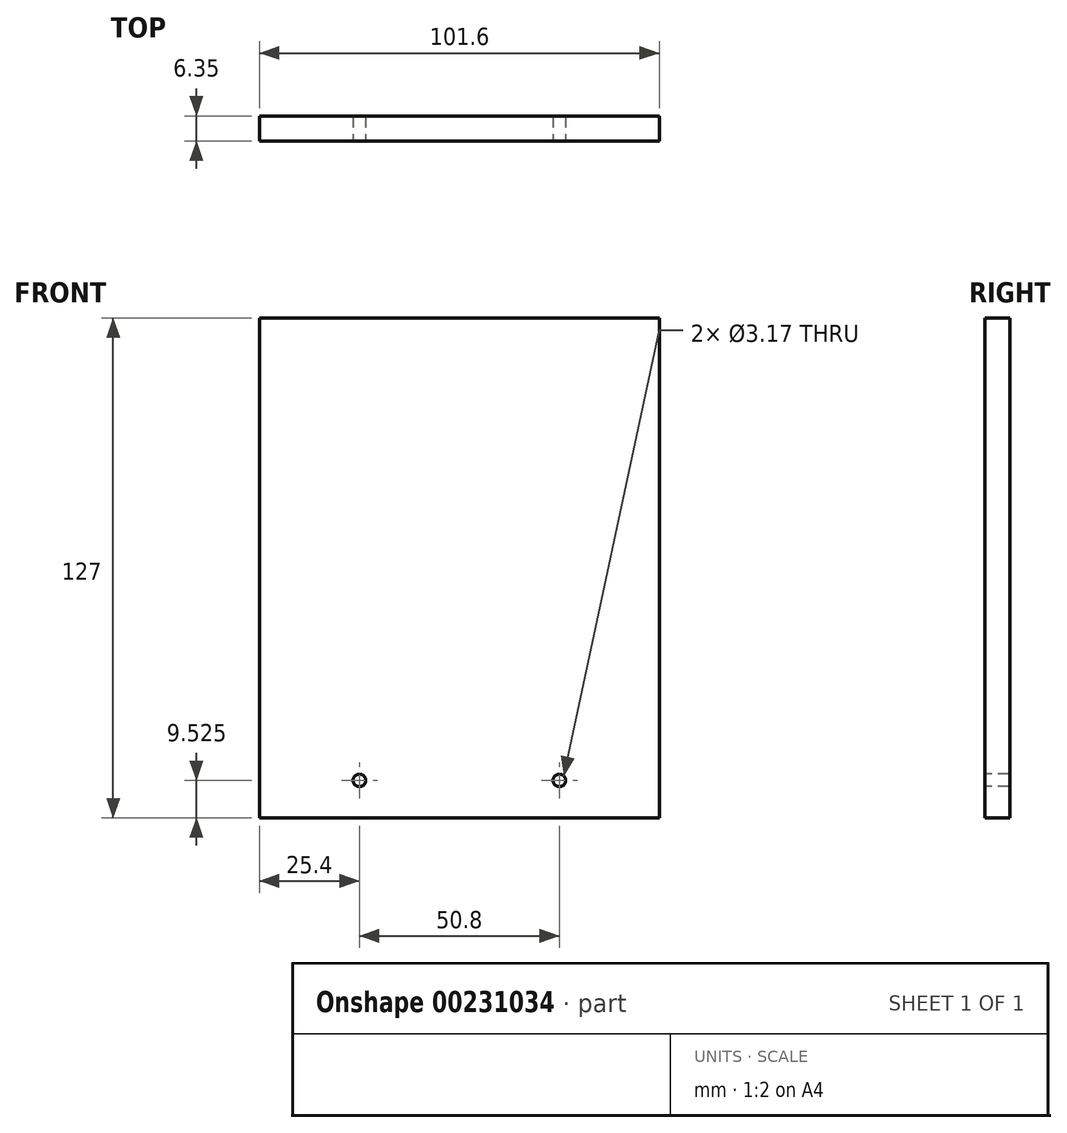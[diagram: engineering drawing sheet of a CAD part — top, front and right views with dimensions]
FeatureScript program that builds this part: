
annotation { "Feature Type Name" : "Feature", "Feature Type Description" : "" }
export const myFeature = defineFeature(function(context is Context, id is Id, definition is map)
    precondition{}
    {
        {
            var Q0;
            Q0=qCreatedBy(makeId("Front.planeOp"),FACE);
            var sketch = newSketch(context, id + "F0", { "sketchPlane" : qUnion([Q0])});
            skLineSegment(sketch, "E0.bottom", {"start": v(50.8, 63.5) * mm, "end": v(-50.8, 63.5) * mm});
            skLineSegment(sketch, "E0.top", {"start": v(50.8, -63.5) * mm, "end": v(-50.8, -63.5) * mm});
            skLineSegment(sketch, "E0.left", {"start": v(50.8, 63.5) * mm, "end": v(50.8, -63.5) * mm});
            skLineSegment(sketch, "E0.right", {"start": v(-50.8, 63.5) * mm, "end": v(-50.8, -63.5) * mm});
            skPoint(sketch, "E0.middle", {"position": v(0, 0) * mm});
            skSolve(sketch);
        }
        {
            var Q0;
            Q0=makeQuery(id+"F0.imprint","IMPRINT",FACE,{"disambiguationData":[TD([[makeQuery(id+"F0.imprint","IMPRINT",EDGE,{"derivedFrom":sQuery(id+"F0.wireOp",EDGE,"E0.bottom")}),1.0]])]});
            extrude(context, id + "F1", {"entities" : qUnion([Q0]), "oppositeDirection" : true, "depth" : 6.35 * mm});
        }
        {
            var Q0;
            Q0=qCreatedBy(makeId("Front.planeOp"),FACE);
            var sketch = newSketch(context, id + "F2", { "sketchPlane" : qUnion([Q0])});
            skCircle(sketch, "E1", {"center": v(-25.4, -53.98) * mm, "radius": 1.59 * mm});
            skCircle(sketch, "E2", {"center": v(25.4, -53.97) * mm, "radius": 1.59 * mm});
            skLineSegment(sketch, "E3", {"start": v(50.8, 63.5) * mm, "end": v(50.8, -38.1) * mm});
            skLineSegment(sketch, "E4", {"start": v(50.8, -38.1) * mm, "end": v(50.8, -44.45) * mm});
            skLineSegment(sketch, "E5", {"start": v(50.8, -44.45) * mm, "end": v(50.8, -53.97) * mm});
            skLineSegment(sketch, "E6", {"start": v(50.8, -53.97) * mm, "end": v(-50.8, -53.97) * mm});
            skSolve(sketch);
        }
        {
            var Q0;
            Q0 = qSketchRegion(id + "F2", true);
            extrude(context, id + "F3", {"entities" : qUnion([Q0]), "operationType" : NewBodyOperationType.REMOVE, "endBound" : BoundingType.THROUGH_ALL, "oppositeDirection" : true, "depth" : 25.4 * mm});
        }
    });
